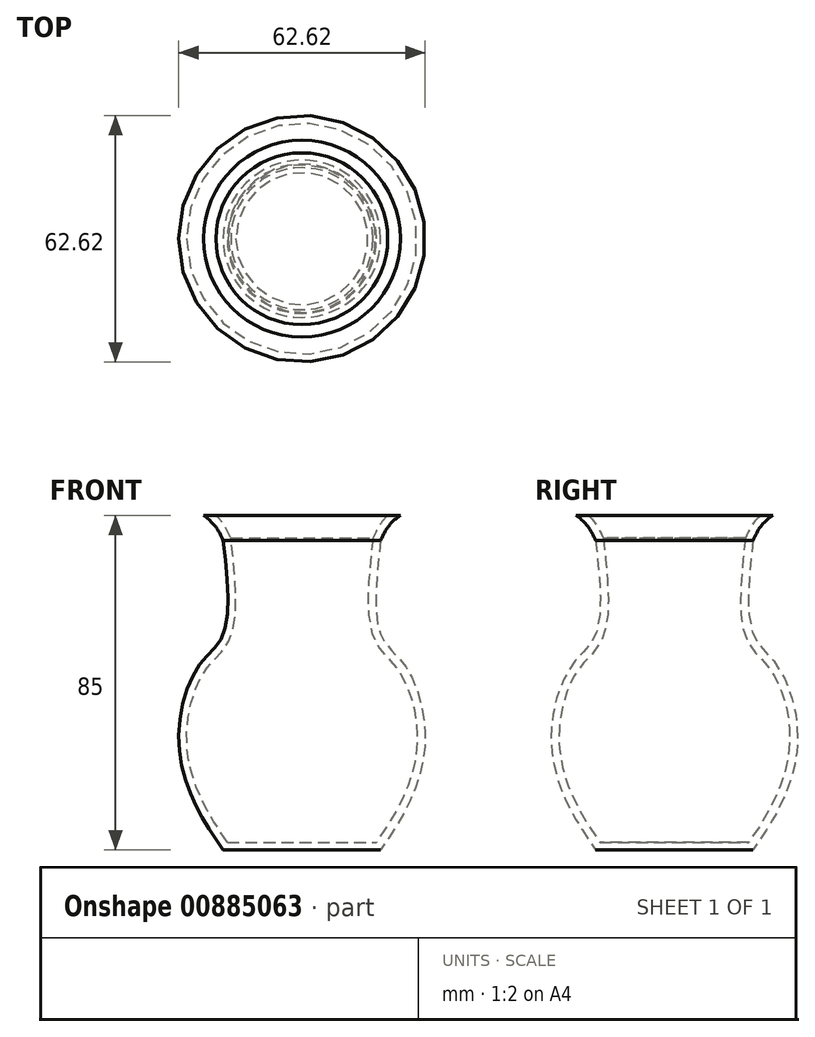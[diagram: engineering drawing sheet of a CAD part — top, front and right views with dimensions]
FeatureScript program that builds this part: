
annotation { "Feature Type Name" : "Feature", "Feature Type Description" : "" }
export const myFeature = defineFeature(function(context is Context, id is Id, definition is map)
    precondition{}
    {
        {
            var Q0;
            Q0=qCreatedBy(makeId("Front.planeOp"),FACE);
            var sketch = newSketch(context, id + "F0", { "sketchPlane" : qUnion([Q0])});
            skPoint(sketch, "E0", {"position": v(0, 0) * mm});
            skLineSegment(sketch, "E1", {"start": v(0, 0) * mm, "end": v(0, 85) * mm});
            skLineSegment(sketch, "E2", {"start": v(0, 0) * mm, "end": v(-20, 0) * mm});
            skFitSpline(sketch, "E3", {"points": [v(-20, 0) * mm, v(-27.26, 11.98) * mm, v(-31.3, 29.16) * mm, v(-26.25, 46.68) * mm, v(-20, 54.76) * mm, v(-20, 78.68) * mm], "startDerivative": vector(-41.93, 61.26) * mm, "endDerivative": vector(-12.97, 116.74) * mm});
            skLineSegment(sketch, "E4", {"start": v(0, 85) * mm, "end": v(-25, 85) * mm});
            skFitSpline(sketch, "E5", {"points": [v(-20, 78.68) * mm, v(-25, 85) * mm, v(-68.36, 97.55) * mm], "startDerivative": vector(-10.18, 21.78) * mm, "endDerivative": vector(-77.44, 16.65) * mm});
            skSolve(sketch);
        }
        {
            var Q0;
            Q0=makeQuery(id+"F0.imprint","IMPRINT",FACE,{"disambiguationData":[TD([[makeQuery(id+"F0.imprint","IMPRINT",EDGE,{"derivedFrom":sQuery(id+"F0.wireOp",EDGE,"E1")}),1.0]])]});
            var Q1;
            Q1=sQuery(id+"F0.wireOp",EDGE,"E1");
            revolve(context, id + "F1", {"surfaceOperationType" : NewSurfaceOperationType.NEW, "entities" : qUnion([Q0]), "axis" : qUnion([Q1]), "revolveType" : RevolveType.FULL});
        }
        {
            var Q0;
            Q0=makeQuery(id+"F1.opRevolve","SWEPT_FACE",FACE,{"disambiguationData":[OSD([sQuery(id+"F0.wireOp",EDGE,"E4")])]});
            shell(context, id + "F2", {"entities" : qUnion([Q0]), "thickness" : 2 * mm});
        }
    });
